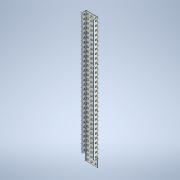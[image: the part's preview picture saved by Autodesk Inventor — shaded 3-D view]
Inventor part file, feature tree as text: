
AUTODESK INVENTOR PART (.ipt)
format: ipt  version: 2020 (Build 240168000, 168)  size: 1,439,232 bytes
history: native  units: in
note: dims shown in document units (in); Inventor stores cm internally (conversion verified against a paired STEP export)
features: other x159, plane x5, pattern_linear x3, split x2, sketch x1, sheet_metal_op x1
ambient origin geometry x8: Origin, YZ Plane, XZ Plane, XY Plane, X Axis, Y Axis, Z Axis, Center Point
bodies: Solid1 (feature_tree)
feature tree (171):
  plane  "Work Plane2"
  plane  "Work Plane1"
  other  "Work Point1"
  other  "Work Point2"
  other  "Work Axis1"
  other  "Work Axis2"
  other  "Work Axis3"
  pattern_linear  "Rectangular Pattern1"  Count1=30 Spacing1=0.5in
  pattern_linear  "Rectangular Pattern2"  Count1=30 Spacing1=0.5in
  pattern_linear  "Rectangular Pattern3"  Count1=32 Spacing1=0.5in
  plane  "Work Plane5"
  split  "Split1"
  split  "Split2"
  plane  "Work Plane3"
  plane  "Work Plane4"
  other  "Work Point3"
  other  "Work Axis4"
  other  "Work Axis5"
  other  "Work Axis6"
  other  "Work Axis7"
  other  "Work Axis8"
  other  "Work Axis9"
  other  "Work Axis10"
  other  "Work Axis11"
  other  "Work Axis12"
  other  "Work Axis13"
  other  "Work Axis14"
  other  "Work Axis15"
  other  "Work Axis16"
  other  "Work Axis17"
  other  "Work Axis18"
  other  "Work Axis19"
  other  "Work Axis20"
  other  "Work Axis21"
  other  "Work Axis22"
  other  "Work Axis23"
  other  "Work Axis24"
  other  "Work Axis25"
  other  "Work Axis26"
  other  "Work Axis27"
  other  "Work Axis28"
  other  "Work Axis29"
  other  "Work Axis30"
  other  "Work Axis31"
  other  "Work Axis32"
  other  "Work Axis38"
  other  "Work Axis39"
  other  "Work Axis40"
  other  "Work Axis41"
  other  "Work Axis42"
  other  "Work Axis43"
  other  "Work Axis44"
  other  "Work Axis45"
  other  "Work Axis46"
  other  "Work Axis47"
  other  "Work Axis48"
  other  "Work Axis49"
  other  "Work Axis50"
  other  "Work Axis51"
  other  "Work Axis52"
  other  "Work Axis53"
  other  "Work Axis54"
  other  "Work Axis55"
  other  "Work Axis56"
  other  "Work Axis57"
  other  "Work Axis58"
  other  "Work Axis59"
  other  "Work Axis60"
  other  "Work Axis61"
  other  "Work Axis62"
  other  "Work Axis63"
  other  "Work Axis64"
  other  "Work Axis65"
  other  "Work Axis66"
  other  "Work Axis72"
  other  "Work Axis73"
  other  "Work Axis74"
  other  "Work Axis75"
  other  "Work Axis76"
  other  "Work Axis77"
  other  "Work Axis78"
  other  "Work Axis79"
  other  "Work Axis80"
  other  "Work Axis81"
  other  "Work Axis82"
  other  "Work Axis83"
  other  "Work Axis84"
  other  "Work Axis85"
  other  "Work Axis86"
  other  "Work Axis87"
  other  "Work Axis88"
  other  "Work Axis89"
  other  "Work Axis90"
  other  "Work Axis91"
  other  "Work Axis92"
  other  "Work Axis93"
  other  "Work Axis94"
  other  "Work Axis95"
  other  "Work Axis96"
  other  "Work Axis97"
  other  "Work Axis98"
  other  "Work Axis99"
  other  "Work Axis100"
  other  "Work Axis101"
  other  "Work Axis102"
  other  "Work Axis106"
  other  "Work Axis107"
  other  "Work Axis108"
  other  "Work Axis109"
  other  "Work Axis110"
  other  "Work Axis111"
  other  "Work Axis112"
  other  "Work Axis113"
  other  "Work Axis114"
  other  "Work Axis115"
  other  "Work Axis116"
  other  "Work Axis117"
  other  "Work Axis118"
  other  "Work Axis119"
  other  "Work Axis120"
  other  "Work Axis121"
  other  "Work Axis122"
  other  "Work Axis123"
  other  "Work Axis124"
  other  "Work Axis125"
  other  "Work Axis126"
  other  "Work Axis127"
  other  "Work Axis128"
  other  "Work Axis129"
  other  "Work Axis130"
  other  "Work Axis131"
  other  "Work Axis132"
  other  "Work Axis133"
  other  "Work Axis134"
  other  "Work Axis135"
  other  "Work Axis136"
  other  "Work Axis137"
  other  "Work Axis141"
  other  "Work Axis142"
  other  "Work Axis143"
  other  "Work Axis144"
  other  "Work Axis145"
  other  "Work Axis146"
  other  "Work Axis147"
  other  "Work Axis148"
  other  "Work Axis149"
  other  "Work Axis150"
  other  "Work Axis151"
  other  "Work Axis152"
  other  "Work Axis153"
  other  "Work Axis154"
  other  "Work Axis155"
  other  "Work Axis156"
  other  "Work Axis157"
  other  "Work Axis158"
  other  "Work Axis159"
  other  "Work Axis160"
  other  "Work Axis161"
  other  "Work Axis162"
  other  "Work Axis163"
  other  "Work Axis164"
  other  "Work Axis165"
  other  "Work Axis166"
  other  "Work Axis167"
  other  "Work Axis168"
  other  "Work Axis169"
  other  "Work Axis170"
  other  "Work Axis171"
  other  "Work Axis172"
  sketch  "Sketch2"  dims[d9=1.1811in d11=0.5in]
  sheet_metal_op  "Fold1"
